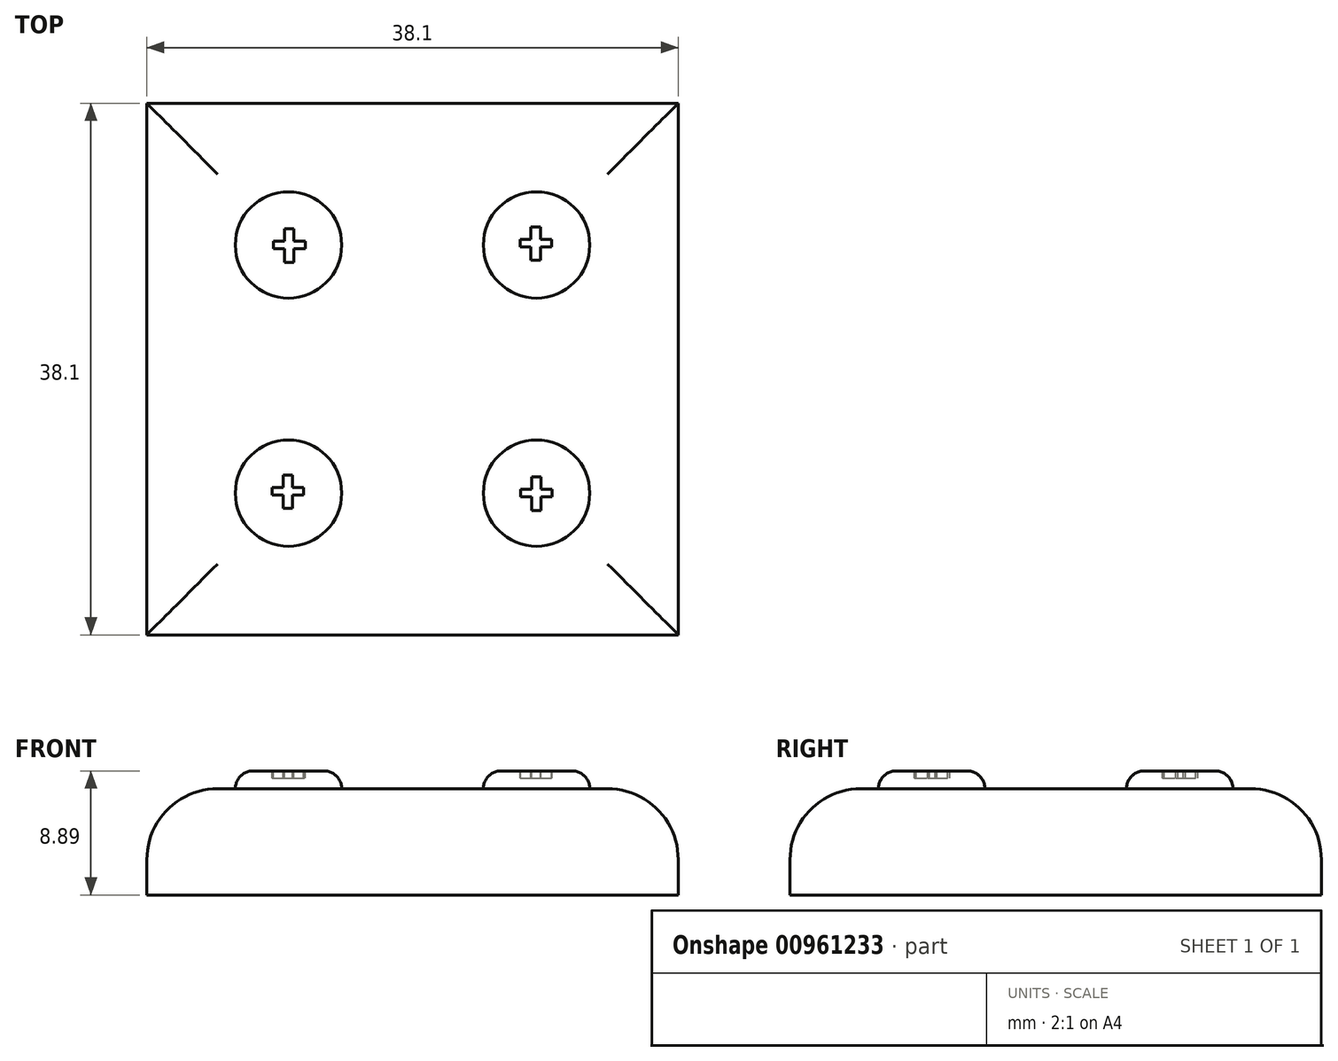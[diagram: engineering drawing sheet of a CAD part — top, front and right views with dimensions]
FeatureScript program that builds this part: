
annotation { "Feature Type Name" : "Feature", "Feature Type Description" : "" }
export const myFeature = defineFeature(function(context is Context, id is Id, definition is map)
    precondition{}
    {
        {
            var Q0;
            Q0=qCreatedBy(makeId("Top.planeOp"),FACE);
            var sketch = newSketch(context, id + "F0", { "sketchPlane" : qUnion([Q0])});
            skLineSegment(sketch, "E0.bottom", {"start": v(19.05, 19.05) * mm, "end": v(-19.05, 19.05) * mm});
            skLineSegment(sketch, "E0.top", {"start": v(19.05, -19.05) * mm, "end": v(-19.05, -19.05) * mm});
            skLineSegment(sketch, "E0.left", {"start": v(19.05, 19.05) * mm, "end": v(19.05, -19.05) * mm});
            skLineSegment(sketch, "E0.right", {"start": v(-19.05, 19.05) * mm, "end": v(-19.05, -19.05) * mm});
            skPoint(sketch, "E0.middle", {"position": v(0, 0) * mm});
            skSolve(sketch);
        }
        {
            var Q0;
            Q0=makeQuery(id+"F0.imprint","IMPRINT",FACE,{"disambiguationData":[TD([[makeQuery(id+"F0.imprint","IMPRINT",EDGE,{"derivedFrom":sQuery(id+"F0.wireOp",EDGE,"E0.bottom")}),1.0]])]});
            extrude(context, id + "F1", {"entities" : qUnion([Q0]), "depth" : 7.62 * mm, "offsetDistance" : 25.4 * mm});
        }
        {
            var Q0;
            Q0=makeQuery(id+"F1.opExtrude","CAP_EDGE",EDGE,{"disambiguationData":[OSD([sQuery(id+"F0.wireOp",EDGE,"E0.right")])],"isStart":false});
            var Q1;
            Q1=makeQuery(id+"F1.opExtrude","CAP_EDGE",EDGE,{"disambiguationData":[OSD([sQuery(id+"F0.wireOp",EDGE,"E0.bottom")])],"isStart":false});
            var Q2;
            Q2=makeQuery(id+"F1.opExtrude","CAP_EDGE",EDGE,{"disambiguationData":[OSD([sQuery(id+"F0.wireOp",EDGE,"E0.left")])],"isStart":false});
            var Q3;
            Q3=makeQuery(id+"F1.opExtrude","CAP_EDGE",EDGE,{"disambiguationData":[OSD([sQuery(id+"F0.wireOp",EDGE,"E0.top")])],"isStart":false});
            fillet(context, id + "F2", {"entities" : qUnion([Q0, Q1, Q2, Q3]), "radius" : 5.08 * mm, "tangentPropagation" : true, "allowEdgeOverflow" : false});
        }
        {
            var Q0;
            Q0=makeQuery(id+"F1.opExtrude","CAP_FACE",FACE,{"disambiguationData":[OSD([sQuery(id+"F0.wireOp",EDGE,"E0.bottom"),sQuery(id+"F0.wireOp",EDGE,"E0.top"),sQuery(id+"F0.wireOp",EDGE,"E0.left"),sQuery(id+"F0.wireOp",EDGE,"E0.right")])],"isStart":false});
            var sketch = newSketch(context, id + "F3", { "sketchPlane" : qUnion([Q0])});
            skPoint(sketch, "E1.middle", {"position": v(0, 0) * mm});
            skCircle(sketch, "E2", {"center": v(-8.9, 8.9) * mm, "radius": 3.81 * mm});
            skCircle(sketch, "E3", {"center": v(8.9, 8.9) * mm, "radius": 3.81 * mm});
            skCircle(sketch, "E4", {"center": v(8.9, -8.9) * mm, "radius": 3.81 * mm});
            skCircle(sketch, "E5", {"center": v(-8.9, -8.9) * mm, "radius": 3.81 * mm});
            skCircle(sketch, "E6", {"center": v(0, 0) * mm, "radius": 6.35 * mm});
            skSolve(sketch);
        }
        {
            var Q0;
            Q0=makeQuery(id+"F3.imprint","IMPRINT",FACE,{"disambiguationData":[TD([[makeQuery(id+"F3.imprint","IMPRINT",EDGE,{"derivedFrom":sQuery(id+"F3.wireOp",EDGE,"E3")}),1.0]])]});
            var Q1;
            Q1=makeQuery(id+"F3.imprint","IMPRINT",FACE,{"disambiguationData":[TD([[makeQuery(id+"F3.imprint","IMPRINT",EDGE,{"derivedFrom":sQuery(id+"F3.wireOp",EDGE,"E4")}),1.0]])]});
            var Q2;
            Q2=makeQuery(id+"F3.imprint","IMPRINT",FACE,{"disambiguationData":[TD([[makeQuery(id+"F3.imprint","IMPRINT",EDGE,{"derivedFrom":sQuery(id+"F3.wireOp",EDGE,"E5")}),1.0]])]});
            var Q3;
            Q3=makeQuery(id+"F3.imprint","IMPRINT",FACE,{"disambiguationData":[TD([[makeQuery(id+"F3.imprint","IMPRINT",EDGE,{"derivedFrom":sQuery(id+"F3.wireOp",EDGE,"E2")}),1.0]])]});
            extrude(context, id + "F4", {"entities" : qUnion([Q0, Q1, Q2, Q3]), "depth" : 1.27 * mm, "offsetDistance" : 25.4 * mm});
        }
        {
            var Q0;
            Q0=makeQuery(id+"F4.opExtrude","CAP_EDGE",EDGE,{"disambiguationData":[OSD([sQuery(id+"F3.wireOp",EDGE,"E2")])],"isStart":false});
            var Q1;
            Q1=makeQuery(id+"F4.opExtrude","CAP_EDGE",EDGE,{"disambiguationData":[OSD([sQuery(id+"F3.wireOp",EDGE,"E3")])],"isStart":false});
            var Q2;
            Q2=makeQuery(id+"F4.opExtrude","CAP_EDGE",EDGE,{"disambiguationData":[OSD([sQuery(id+"F3.wireOp",EDGE,"E4")])],"isStart":false});
            var Q3;
            Q3=makeQuery(id+"F4.opExtrude","CAP_EDGE",EDGE,{"disambiguationData":[OSD([sQuery(id+"F3.wireOp",EDGE,"E5")])],"isStart":false});
            fillet(context, id + "F5", {"entities" : qUnion([Q0, Q1, Q2, Q3]), "radius" : 1.27 * mm, "tangentPropagation" : true, "allowEdgeOverflow" : false});
        }
        {
            var Q0;
            Q0=makeQuery(id+"F4.opExtrude","CAP_FACE",FACE,{"disambiguationData":[OSD([sQuery(id+"F3.wireOp",EDGE,"E2")])],"isStart":false});
            var sketch = newSketch(context, id + "F6", { "sketchPlane" : qUnion([Q0])});
            skLineSegment(sketch, "E7.bottom", {"start": v(-9.18, 7.65) * mm, "end": v(-8.5, 7.65) * mm});
            skLineSegment(sketch, "E7.top", {"start": v(-9.18, 10.04) * mm, "end": v(-8.5, 10.04) * mm});
            skLineSegment(sketch, "E7.left", {"start": v(-9.18, 7.65) * mm, "end": v(-9.18, 10.04) * mm});
            skLineSegment(sketch, "E7.right", {"start": v(-8.5, 7.65) * mm, "end": v(-8.5, 10.04) * mm});
            skLineSegment(sketch, "E8.bottom", {"start": v(-9.96, 8.6) * mm, "end": v(-7.7, 8.6) * mm});
            skLineSegment(sketch, "E8.top", {"start": v(-9.96, 9.15) * mm, "end": v(-7.7, 9.15) * mm});
            skLineSegment(sketch, "E8.left", {"start": v(-9.96, 8.6) * mm, "end": v(-9.96, 9.15) * mm});
            skLineSegment(sketch, "E8.right", {"start": v(-7.7, 8.6) * mm, "end": v(-7.7, 9.15) * mm});
            skLineSegment(sketch, "E9.bottom", {"start": v(8.5, 7.8) * mm, "end": v(9.18, 7.8) * mm});
            skLineSegment(sketch, "E9.top", {"start": v(8.5, 10.19) * mm, "end": v(9.18, 10.19) * mm});
            skLineSegment(sketch, "E9.left", {"start": v(8.5, 7.8) * mm, "end": v(8.5, 10.19) * mm});
            skLineSegment(sketch, "E9.right", {"start": v(9.18, 7.8) * mm, "end": v(9.18, 10.19) * mm});
            skLineSegment(sketch, "E10.bottom", {"start": v(7.71, 8.76) * mm, "end": v(9.98, 8.76) * mm});
            skLineSegment(sketch, "E10.top", {"start": v(7.71, 9.3) * mm, "end": v(9.98, 9.3) * mm});
            skLineSegment(sketch, "E10.left", {"start": v(7.71, 8.76) * mm, "end": v(7.71, 9.3) * mm});
            skLineSegment(sketch, "E10.right", {"start": v(9.98, 8.76) * mm, "end": v(9.98, 9.3) * mm});
            skLineSegment(sketch, "E11.bottom", {"start": v(-9.28, -10) * mm, "end": v(-8.6, -10) * mm});
            skLineSegment(sketch, "E11.top", {"start": v(-9.28, -7.6) * mm, "end": v(-8.6, -7.6) * mm});
            skLineSegment(sketch, "E11.left", {"start": v(-9.28, -10) * mm, "end": v(-9.28, -7.6) * mm});
            skLineSegment(sketch, "E11.right", {"start": v(-8.6, -10) * mm, "end": v(-8.6, -7.6) * mm});
            skLineSegment(sketch, "E12.bottom", {"start": v(-10.06, -9.03) * mm, "end": v(-7.8, -9.03) * mm});
            skLineSegment(sketch, "E12.top", {"start": v(-10.06, -8.5) * mm, "end": v(-7.8, -8.5) * mm});
            skLineSegment(sketch, "E12.left", {"start": v(-10.06, -9.03) * mm, "end": v(-10.06, -8.5) * mm});
            skLineSegment(sketch, "E12.right", {"start": v(-7.8, -9.03) * mm, "end": v(-7.8, -8.5) * mm});
            skLineSegment(sketch, "E13.bottom", {"start": v(8.53, -10.13) * mm, "end": v(9.21, -10.13) * mm});
            skLineSegment(sketch, "E13.top", {"start": v(8.53, -7.74) * mm, "end": v(9.21, -7.74) * mm});
            skLineSegment(sketch, "E13.left", {"start": v(8.53, -10.13) * mm, "end": v(8.53, -7.74) * mm});
            skLineSegment(sketch, "E13.right", {"start": v(9.21, -10.13) * mm, "end": v(9.21, -7.74) * mm});
            skLineSegment(sketch, "E14.bottom", {"start": v(7.74, -9.17) * mm, "end": v(10, -9.17) * mm});
            skLineSegment(sketch, "E14.top", {"start": v(7.74, -8.63) * mm, "end": v(10, -8.63) * mm});
            skLineSegment(sketch, "E14.left", {"start": v(7.74, -9.17) * mm, "end": v(7.74, -8.63) * mm});
            skLineSegment(sketch, "E14.right", {"start": v(10, -9.17) * mm, "end": v(10, -8.63) * mm});
            skSolve(sketch);
        }
        {
            var Q0;
            {var subQ0=sQuery(id+"F6.wireOp",EDGE,"E7.top");Q0=makeQuery(id+"F6.imprint","IMPRINT",FACE,{"disambiguationData":[TD([[makeQuery(id+"F6.imprint","IMPRINT",EDGE,{"derivedFrom":subQ0}),-1.0]])]});}
            var Q1;
            {var subQ5=sQuery(id+"F6.wireOp",EDGE,"E8.left");Q1=makeQuery(id+"F6.imprint","IMPRINT",FACE,{"disambiguationData":[TD([[makeQuery(id+"F6.imprint","IMPRINT",EDGE,{"derivedFrom":subQ5}),-1.0]])]});}
            var Q2;
            {var subQ0=sQuery(id+"F6.wireOp",EDGE,"E8.bottom");var subQ1=sQuery(id+"F6.wireOp",EDGE,"E7.left");var subQ2=makeQuery(id+"F6.imprint","INTERSECT",VERTEX,{"derivedFrom":[subQ1,subQ0]});Q2=makeQuery(id+"F6.imprint","IMPRINT",FACE,{"disambiguationData":[TD([[makeQuery(id+"F6.imprint","IMPRINT",EDGE,{"disambiguationData":[TD([[subQ2,-1.0]])],"derivedFrom":subQ1}),-1.0]])]});}
            var Q3;
            {var subQ5=sQuery(id+"F6.wireOp",EDGE,"E8.right");Q3=makeQuery(id+"F6.imprint","IMPRINT",FACE,{"disambiguationData":[TD([[makeQuery(id+"F6.imprint","IMPRINT",EDGE,{"derivedFrom":subQ5}),1.0]])]});}
            var Q4;
            {var subQ0=sQuery(id+"F6.wireOp",EDGE,"E7.bottom");Q4=makeQuery(id+"F6.imprint","IMPRINT",FACE,{"disambiguationData":[TD([[makeQuery(id+"F6.imprint","IMPRINT",EDGE,{"derivedFrom":subQ0}),1.0]])]});}
            var Q5;
            {var subQ0=sQuery(id+"F6.wireOp",EDGE,"E9.bottom");Q5=makeQuery(id+"F6.imprint","IMPRINT",FACE,{"disambiguationData":[TD([[makeQuery(id+"F6.imprint","IMPRINT",EDGE,{"derivedFrom":subQ0}),1.0]])]});}
            var Q6;
            {var subQ5=sQuery(id+"F6.wireOp",EDGE,"E10.left");Q6=makeQuery(id+"F6.imprint","IMPRINT",FACE,{"disambiguationData":[TD([[makeQuery(id+"F6.imprint","IMPRINT",EDGE,{"derivedFrom":subQ5}),-1.0]])]});}
            var Q7;
            {var subQ0=sQuery(id+"F6.wireOp",EDGE,"E10.bottom");var subQ1=sQuery(id+"F6.wireOp",EDGE,"E9.left");var subQ2=makeQuery(id+"F6.imprint","INTERSECT",VERTEX,{"derivedFrom":[subQ1,subQ0]});Q7=makeQuery(id+"F6.imprint","IMPRINT",FACE,{"disambiguationData":[TD([[makeQuery(id+"F6.imprint","IMPRINT",EDGE,{"disambiguationData":[TD([[subQ2,-1.0]])],"derivedFrom":subQ1}),-1.0]])]});}
            var Q8;
            {var subQ0=sQuery(id+"F6.wireOp",EDGE,"E9.top");Q8=makeQuery(id+"F6.imprint","IMPRINT",FACE,{"disambiguationData":[TD([[makeQuery(id+"F6.imprint","IMPRINT",EDGE,{"derivedFrom":subQ0}),-1.0]])]});}
            var Q9;
            {var subQ5=sQuery(id+"F6.wireOp",EDGE,"E10.right");Q9=makeQuery(id+"F6.imprint","IMPRINT",FACE,{"disambiguationData":[TD([[makeQuery(id+"F6.imprint","IMPRINT",EDGE,{"derivedFrom":subQ5}),1.0]])]});}
            var Q10;
            {var subQ5=sQuery(id+"F6.wireOp",EDGE,"E12.left");Q10=makeQuery(id+"F6.imprint","IMPRINT",FACE,{"disambiguationData":[TD([[makeQuery(id+"F6.imprint","IMPRINT",EDGE,{"derivedFrom":subQ5}),-1.0]])]});}
            var Q11;
            {var subQ0=sQuery(id+"F6.wireOp",EDGE,"E12.bottom");var subQ1=sQuery(id+"F6.wireOp",EDGE,"E11.left");var subQ2=makeQuery(id+"F6.imprint","INTERSECT",VERTEX,{"derivedFrom":[subQ1,subQ0]});Q11=makeQuery(id+"F6.imprint","IMPRINT",FACE,{"disambiguationData":[TD([[makeQuery(id+"F6.imprint","IMPRINT",EDGE,{"disambiguationData":[TD([[subQ2,-1.0]])],"derivedFrom":subQ1}),-1.0]])]});}
            var Q12;
            {var subQ0=sQuery(id+"F6.wireOp",EDGE,"E11.top");Q12=makeQuery(id+"F6.imprint","IMPRINT",FACE,{"disambiguationData":[TD([[makeQuery(id+"F6.imprint","IMPRINT",EDGE,{"derivedFrom":subQ0}),-1.0]])]});}
            var Q13;
            {var subQ5=sQuery(id+"F6.wireOp",EDGE,"E12.right");Q13=makeQuery(id+"F6.imprint","IMPRINT",FACE,{"disambiguationData":[TD([[makeQuery(id+"F6.imprint","IMPRINT",EDGE,{"derivedFrom":subQ5}),1.0]])]});}
            var Q14;
            {var subQ0=sQuery(id+"F6.wireOp",EDGE,"E13.bottom");Q14=makeQuery(id+"F6.imprint","IMPRINT",FACE,{"disambiguationData":[TD([[makeQuery(id+"F6.imprint","IMPRINT",EDGE,{"derivedFrom":subQ0}),1.0]])]});}
            var Q15;
            {var subQ5=sQuery(id+"F6.wireOp",EDGE,"E14.left");Q15=makeQuery(id+"F6.imprint","IMPRINT",FACE,{"disambiguationData":[TD([[makeQuery(id+"F6.imprint","IMPRINT",EDGE,{"derivedFrom":subQ5}),-1.0]])]});}
            var Q16;
            {var subQ5=sQuery(id+"F6.wireOp",EDGE,"E14.right");Q16=makeQuery(id+"F6.imprint","IMPRINT",FACE,{"disambiguationData":[TD([[makeQuery(id+"F6.imprint","IMPRINT",EDGE,{"derivedFrom":subQ5}),1.0]])]});}
            var Q17;
            {var subQ0=sQuery(id+"F6.wireOp",EDGE,"E13.top");Q17=makeQuery(id+"F6.imprint","IMPRINT",FACE,{"disambiguationData":[TD([[makeQuery(id+"F6.imprint","IMPRINT",EDGE,{"derivedFrom":subQ0}),-1.0]])]});}
            var Q18;
            {var subQ0=sQuery(id+"F6.wireOp",EDGE,"E14.bottom");var subQ1=sQuery(id+"F6.wireOp",EDGE,"E13.left");var subQ2=makeQuery(id+"F6.imprint","INTERSECT",VERTEX,{"derivedFrom":[subQ1,subQ0]});Q18=makeQuery(id+"F6.imprint","IMPRINT",FACE,{"disambiguationData":[TD([[makeQuery(id+"F6.imprint","IMPRINT",EDGE,{"disambiguationData":[TD([[subQ2,-1.0]])],"derivedFrom":subQ1}),-1.0]])]});}
            var Q19;
            {var subQ0=sQuery(id+"F6.wireOp",EDGE,"E11.bottom");Q19=makeQuery(id+"F6.imprint","IMPRINT",FACE,{"disambiguationData":[TD([[makeQuery(id+"F6.imprint","IMPRINT",EDGE,{"derivedFrom":subQ0}),1.0]])]});}
            var Q20;
            Q20 = qConstructionFilter(qBodyType(qCreatedBy(id + "F6" ,EDGE), BodyType.WIRE), ConstructionObject.NO);
            extrude(context, id + "F7", {"entities" : qUnion([Q0, Q1, Q2, Q3, Q4, Q5, Q6, Q7, Q8, Q9, Q10, Q11, Q12, Q13, Q14, Q15, Q16, Q17, Q18, Q19]), "operationType" : NewBodyOperationType.REMOVE, "surfaceEntities" : qUnion([Q20]), "oppositeDirection" : true, "depth" : 0.5 * mm, "offsetDistance" : 25.4 * mm});
        }
        {
            var Q0;
            Q0 = qSketchRegion(id + "F6", true);
            extrude(context, id + "F8", {"entities" : qUnion([Q0]), "operationType" : NewBodyOperationType.REMOVE, "oppositeDirection" : true, "depth" : 0.5 * mm, "offsetDistance" : 25.4 * mm});
        }
    });
